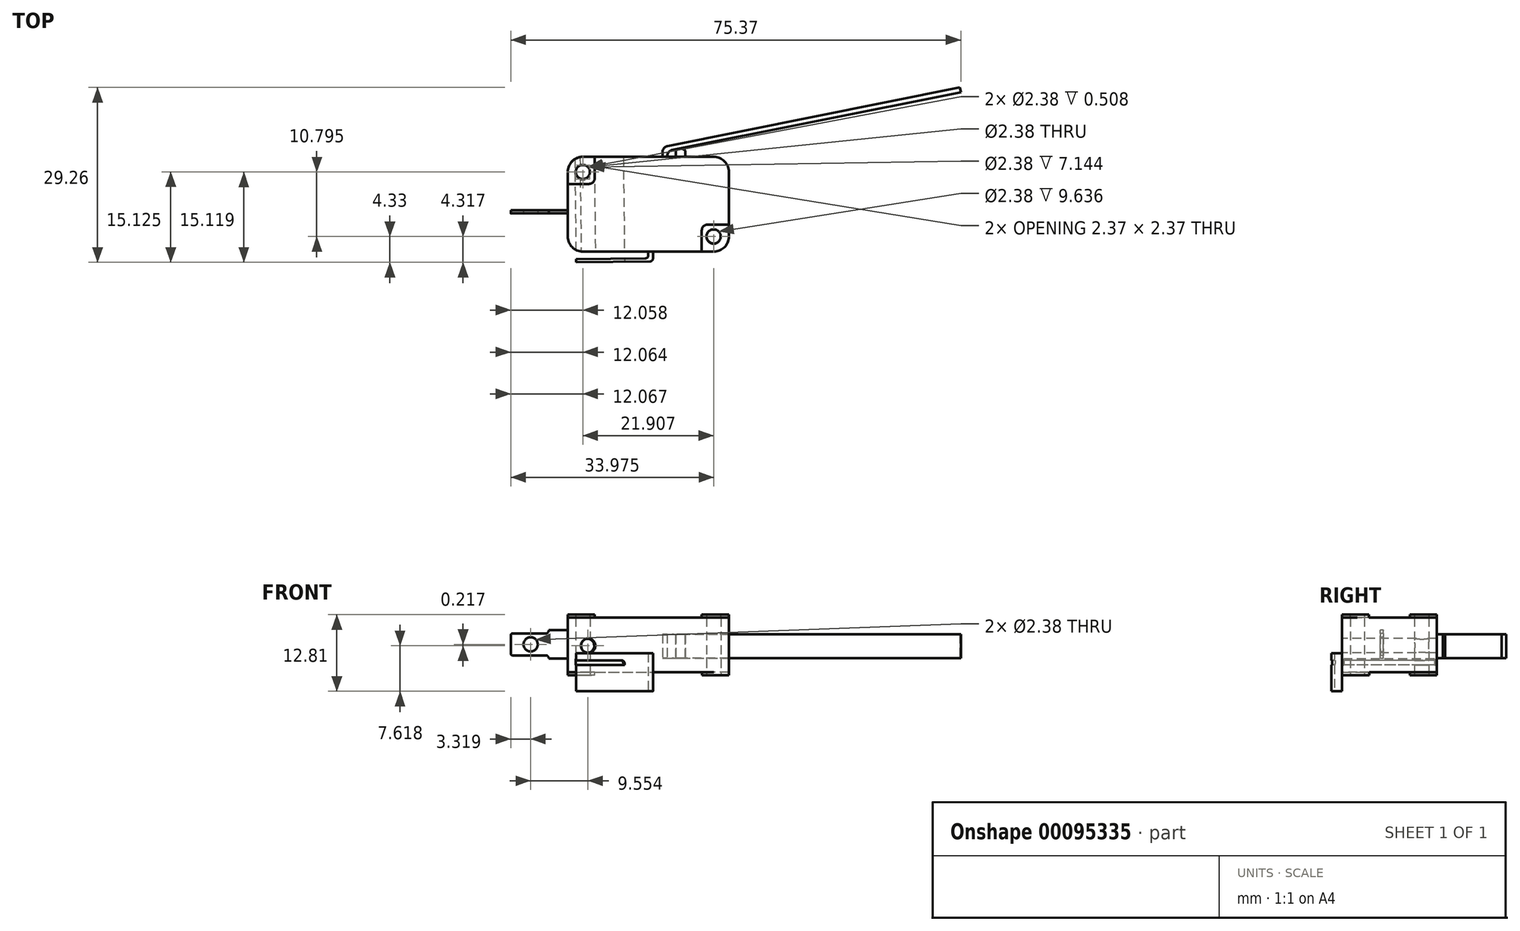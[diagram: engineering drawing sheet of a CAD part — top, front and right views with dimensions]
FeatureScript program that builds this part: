
annotation { "Feature Type Name" : "Feature", "Feature Type Description" : "" }
export const myFeature = defineFeature(function(context is Context, id is Id, definition is map)
    precondition{}
    {
        {
            var Q0;
            Q0=qCreatedBy(makeId("Top.planeOp"),FACE);
            var sketch = newSketch(context, id + "F0", { "sketchPlane" : qUnion([Q0])});
            skLineSegment(sketch, "E0.bottom", {"start": v(-22.21, 9.46) * mm, "end": v(-0.3, 9.46) * mm});
            skLineSegment(sketch, "E0.top", {"start": v(-22.21, -6.42) * mm, "end": v(-0.3, -6.42) * mm});
            skLineSegment(sketch, "E0.left", {"start": v(-24.75, 6.92) * mm, "end": v(-24.75, -3.88) * mm});
            skLineSegment(sketch, "E0.right", {"start": v(2.23, 6.92) * mm, "end": v(2.23, -3.88) * mm});
            skPoint(sketch, "E1.visualSharp", {"position": v(-24.75, 9.46) * mm});
            skArc(sketch, "E1.filletArc", {"start": v(-22.21, 9.46) * mm, "mid": v(-24, 8.71) * mm, "end": v(-24.75, 6.92) * mm});
            skPoint(sketch, "E2.visualSharp", {"position": v(2.23, 9.46) * mm});
            skArc(sketch, "E2.filletArc", {"start": v(2.23, 6.92) * mm, "mid": v(1.5, 8.71) * mm, "end": v(-0.3, 9.46) * mm});
            skPoint(sketch, "E3.visualSharp", {"position": v(2.23, -6.42) * mm});
            skArc(sketch, "E3.filletArc", {"start": v(-0.3, -6.42) * mm, "mid": v(1.5, -5.68) * mm, "end": v(2.23, -3.88) * mm});
            skPoint(sketch, "E4.visualSharp", {"position": v(-24.75, -6.42) * mm});
            skArc(sketch, "E4.filletArc", {"start": v(-24.75, -3.88) * mm, "mid": v(-24, -5.68) * mm, "end": v(-22.21, -6.42) * mm});
            skCircle(sketch, "E5", {"center": v(-22.21, 6.92) * mm, "radius": 1.2 * mm});
            skCircle(sketch, "E6", {"center": v(-0.3, -3.88) * mm, "radius": 1.2 * mm});
            skSolve(sketch);
        }
        {
            var Q0;
            Q0 = qSketchRegion(id + "F0", true);
            extrude(context, id + "F1", {"entities" : qUnion([Q0]), "depth" : 9.13 * mm});
        }
        {
            var Q0;
            Q0=makeQuery(id+"F1.opExtrude","CAP_FACE",FACE,{"disambiguationData":[OSD([sQuery(id+"F0.wireOp",EDGE,"E0.bottom"),sQuery(id+"F0.wireOp",EDGE,"E0.top"),sQuery(id+"F0.wireOp",EDGE,"E0.left"),sQuery(id+"F0.wireOp",EDGE,"E0.right"),sQuery(id+"F0.wireOp",EDGE,"E1.filletArc"),sQuery(id+"F0.wireOp",EDGE,"E2.filletArc"),sQuery(id+"F0.wireOp",EDGE,"E3.filletArc"),sQuery(id+"F0.wireOp",EDGE,"E4.filletArc"),sQuery(id+"F0.wireOp",EDGE,"E5"),sQuery(id+"F0.wireOp",EDGE,"E6")])],"isStart":true});
            cPlane(context, id + "F2", {"entities" : qUnion([Q0]), "cplaneType" : CPlaneType.OFFSET, "offset" : 2.38 * mm, "oppositeDirection" : true, "width" : 152.4 * mm, "height" : 152.4 * mm});
        }
        {
            var Q0;
            Q0=qCreatedBy(id+"F2.planeOp",FACE);
            var sketch = newSketch(context, id + "F3", { "sketchPlane" : qUnion([Q0])});
            skLineSegment(sketch, "E7", {"start": v(-8.88, -9.48) * mm, "end": v(-8.88, -11.07) * mm});
            skLineSegment(sketch, "E8", {"start": v(-8.88, -11.07) * mm, "end": v(40.93, -21.05) * mm});
            skLineSegment(sketch, "E9", {"start": v(40.93, -21.05) * mm, "end": v(41.09, -20.28) * mm});
            skLineSegment(sketch, "E10", {"start": v(41.09, -20.28) * mm, "end": v(-8.08, -10.42) * mm});
            skLineSegment(sketch, "E11", {"start": v(-8.08, -10.42) * mm, "end": v(-8.08, -9.48) * mm});
            skLineSegment(sketch, "E12", {"start": v(-8.08, -9.48) * mm, "end": v(-8.88, -9.48) * mm});
            skSolve(sketch);
        }
        {
            var Q0;
            Q0 = qSketchRegion(id + "F3", true);
            extrude(context, id + "F4", {"entities" : qUnion([Q0]), "oppositeDirection" : true, "depth" : 3.97 * mm});
        }
        {
            var Q0;
            Q0=makeQuery(id+"F4.opExtrude","SWEPT_EDGE",EDGE,{"disambiguationData":[OSD([sQuery(id+"F3.wireOp",EDGE,"E7"),sQuery(id+"F3.wireOp",EDGE,"E8")])]});
            var Q1;
            Q1=makeQuery(id+"F4.opExtrude","SWEPT_EDGE",EDGE,{"disambiguationData":[OSD([sQuery(id+"F3.wireOp",EDGE,"E10"),sQuery(id+"F3.wireOp",EDGE,"E11")])]});
            fillet(context, id + "F5", {"entities" : qUnion([Q0, Q1]), "radius" : 1.02 * mm, "tangentPropagation" : true, "allowEdgeOverflow" : false});
        }
        {
            var Q0;
            Q0=makeQuery(id+"F1.opExtrude","CAP_FACE",FACE,{"disambiguationData":[OSD([sQuery(id+"F0.wireOp",EDGE,"E0.bottom"),sQuery(id+"F0.wireOp",EDGE,"E0.top"),sQuery(id+"F0.wireOp",EDGE,"E0.left"),sQuery(id+"F0.wireOp",EDGE,"E0.right"),sQuery(id+"F0.wireOp",EDGE,"E1.filletArc"),sQuery(id+"F0.wireOp",EDGE,"E2.filletArc"),sQuery(id+"F0.wireOp",EDGE,"E3.filletArc"),sQuery(id+"F0.wireOp",EDGE,"E4.filletArc"),sQuery(id+"F0.wireOp",EDGE,"E5"),sQuery(id+"F0.wireOp",EDGE,"E6")])],"isStart":false});
            var sketch = newSketch(context, id + "F6", { "sketchPlane" : qUnion([Q0])});
            skLineSegment(sketch, "E13.bottom", {"start": v(-22.22, 9.44) * mm, "end": v(-20.24, 9.44) * mm});
            skLineSegment(sketch, "E13.top", {"start": v(-2.3, -6.43) * mm, "end": v(-0.31, -6.43) * mm});
            skLineSegment(sketch, "E13.left", {"start": v(-24.76, 6.9) * mm, "end": v(-24.76, 4.92) * mm});
            skLineSegment(sketch, "E13.right", {"start": v(2.23, -1.9) * mm, "end": v(2.23, -3.9) * mm});
            skPoint(sketch, "E14.visualSharp", {"position": v(-24.76, 9.44) * mm});
            skArc(sketch, "E14.filletArc", {"start": v(-22.22, 9.44) * mm, "mid": v(-24.02, 8.7) * mm, "end": v(-24.76, 6.9) * mm});
            skPoint(sketch, "E15.visualSharp", {"position": v(2.23, 9.44) * mm});
            skPoint(sketch, "E16.visualSharp", {"position": v(2.23, -6.43) * mm});
            skArc(sketch, "E16.filletArc", {"start": v(-0.31, -6.43) * mm, "mid": v(1.48, -5.69) * mm, "end": v(2.23, -3.9) * mm});
            skPoint(sketch, "E17.visualSharp", {"position": v(-24.76, -6.43) * mm});
            skCircle(sketch, "E18", {"center": v(-22.22, 6.9) * mm, "radius": 1.2 * mm});
            skCircle(sketch, "E19", {"center": v(-0.31, -3.9) * mm, "radius": 1.2 * mm});
            skLineSegment(sketch, "E20.bottom", {"start": v(-1.37, -1.9) * mm, "end": v(2.23, -1.9) * mm});
            skLineSegment(sketch, "E20.left", {"start": v(-2.3, -2.84) * mm, "end": v(-2.3, -6.43) * mm});
            skLineSegment(sketch, "E21.top", {"start": v(-24.76, 4.92) * mm, "end": v(-21.17, 4.92) * mm});
            skLineSegment(sketch, "E21.right", {"start": v(-20.24, 9.44) * mm, "end": v(-20.24, 5.85) * mm});
            skPoint(sketch, "E22.visualSharp", {"position": v(-20.24, 4.92) * mm});
            skArc(sketch, "E22.filletArc", {"start": v(-21.17, 4.92) * mm, "mid": v(-20.51, 5.2) * mm, "end": v(-20.24, 5.85) * mm});
            skPoint(sketch, "E23.visualSharp", {"position": v(-2.3, -1.9) * mm});
            skArc(sketch, "E23.filletArc", {"start": v(-1.37, -1.9) * mm, "mid": v(-2.03, -2.18) * mm, "end": v(-2.3, -2.84) * mm});
            skSolve(sketch);
        }
        {
            var Q0;
            Q0 = qSketchRegion(id + "F6", true);
            extrude(context, id + "F7", {"entities" : qUnion([Q0]), "operationType" : NewBodyOperationType.ADD, "depth" : 0.5 * mm});
        }
        {
            var Q0;
            Q0=qCreatedBy(id+"F2.planeOp",FACE);
            var sketch = newSketch(context, id + "F8", { "sketchPlane" : qUnion([Q0])});
            skLineSegment(sketch, "E24.bottom", {"start": v(-5.04, -9.44) * mm, "end": v(-6.67, -9.44) * mm});
            skLineSegment(sketch, "E24.top", {"start": v(-5.04, -10.44) * mm, "end": v(-6.67, -10.44) * mm});
            skLineSegment(sketch, "E24.left", {"start": v(-5.04, -9.44) * mm, "end": v(-5.04, -10.44) * mm});
            skLineSegment(sketch, "E24.right", {"start": v(-6.67, -9.44) * mm, "end": v(-6.67, -10.44) * mm});
            skArc(sketch, "E25", {"start": v(-6.67, -10.44) * mm, "mid": v(-5.86, -10.82) * mm, "end": v(-5.04, -10.44) * mm});
            skSolve(sketch);
        }
        {
            var Q0;
            Q0 = qSketchRegion(id + "F8", true);
            extrude(context, id + "F9", {"entities" : qUnion([Q0]), "operationType" : NewBodyOperationType.ADD, "oppositeDirection" : true, "depth" : 3.97 * mm});
        }
        {
            var Q0;
            Q0=qCreatedBy(makeId("Top.planeOp"),FACE);
            cPlane(context, id + "F10", {"entities" : qUnion([Q0]), "cplaneType" : CPlaneType.OFFSET, "offset" : 2.75 / 406.4 * mm, "width" : 152.4 * mm, "height" : 152.4 * mm});
        }
        {
            var Q0;
            Q0=qCreatedBy(id+"F10.planeOp",FACE);
            var sketch = newSketch(context, id + "F11", { "sketchPlane" : qUnion([Q0])});
            skLineSegment(sketch, "E26", {"start": v(-11.26, -6.43) * mm, "end": v(-11.26, -7.55) * mm});
            skLineSegment(sketch, "E27", {"start": v(-23.36, -8.2) * mm, "end": v(-23.36, -7.7) * mm});
            skLineSegment(sketch, "E28", {"start": v(-23.36, -8.2) * mm, "end": v(-10.47, -8.05) * mm});
            skLineSegment(sketch, "E29", {"start": v(-10.47, -8.05) * mm, "end": v(-10.47, -6.43) * mm});
            skLineSegment(sketch, "E30", {"start": v(-11.26, -6.43) * mm, "end": v(-10.47, -6.43) * mm});
            skLineSegment(sketch, "E31", {"start": v(-10.47, -7.55) * mm, "end": v(-10.47, -6.43) * mm});
            skLineSegment(sketch, "E32", {"start": v(-23.36, -7.7) * mm, "end": v(-11.26, -7.55) * mm});
            skSolve(sketch);
        }
        {
            var Q0;
            Q0=makeQuery(id+"F11.imprint","IMPRINT",FACE,{"disambiguationData":[TD([[makeQuery(id+"F11.imprint","IMPRINT",EDGE,{"derivedFrom":sQuery(id+"F11.wireOp",EDGE,"E26")}),1.0]])]});
            extrude(context, id + "F12", {"entities" : qUnion([Q0]), "depth" : 3.17 * mm, "hasSecondDirection" : true, "secondDirectionOppositeDirection" : true, "secondDirectionDepth" : 3.17 * mm});
        }
        {
            var Q0;
            {var subQ0=sQuery(id+"F11.wireOp",EDGE,"E28");Q0=makeQuery(id+"FmFe5163YoJR6j5_2.boolean.opBoolean","MERGE",FACE,{"derivedFrom":[makeQuery(id+"F12.opExtrude","SWEPT_FACE",FACE,{"disambiguationData":[OSD([subQ0])]}),makeQuery(id+"FmFe5163YoJR6j5_2.opExtrude","SWEPT_FACE",FACE,{"disambiguationData":[OSD([subQ0])]})]});}
            var sketch = newSketch(context, id + "F13", { "sketchPlane" : qUnion([Q0])});
            skCircle(sketch, "E33", {"center": v(-22.31, 4.41) * mm, "radius": 0.82 * mm});
            skSolve(sketch);
        }
        {
            var Q0;
            Q0=makeQuery(id+"F13.imprint","IMPRINT",FACE,{"disambiguationData":[TD([[makeQuery(id+"F13.imprint","IMPRINT",EDGE,{"derivedFrom":sQuery(id+"F13.wireOp",EDGE,"E33")}),1.0]])]});
            extrude(context, id + "F14", {"entities" : qUnion([Q0]), "operationType" : NewBodyOperationType.REMOVE, "oppositeDirection" : true, "depth" : 0.5 * mm});
        }
        {
            var Q0;
            Q0=qCreatedBy(makeId("Front.planeOp"),FACE);
            cPlane(context, id + "F15", {"entities" : qUnion([Q0]), "cplaneType" : CPlaneType.OFFSET, "offset" : 0.03 * mm, "width" : 152.4 * mm, "height" : 152.4 * mm});
        }
        {
            var Q0;
            Q0=qCreatedBy(id+"F15.planeOp",FACE);
            var sketch = newSketch(context, id + "F16", { "sketchPlane" : qUnion([Q0])});
            skLineSegment(sketch, "E34", {"start": v(-24.75, 2.28) * mm, "end": v(-24.75, 7.05) * mm});
            skLineSegment(sketch, "E35", {"start": v(-24.75, 7.05) * mm, "end": v(-27.93, 7.05) * mm});
            skLineSegment(sketch, "E36", {"start": v(-34.28, 6.24) * mm, "end": v(-34.28, 3.1) * mm});
            skLineSegment(sketch, "E37", {"start": v(-27.93, 2.28) * mm, "end": v(-24.75, 2.28) * mm});
            skCircle(sketch, "E38", {"center": v(-30.96, 4.66) * mm, "radius": 1.2 * mm});
            skPoint(sketch, "E39", {"position": v(-34.28, 4.66) * mm});
            skLineSegment(sketch, "E40", {"start": v(-27.93, 7.05) * mm, "end": v(-27.93, 6.5) * mm});
            skLineSegment(sketch, "E41", {"start": v(-27.93, 2.84) * mm, "end": v(-27.93, 2.28) * mm});
            skLineSegment(sketch, "E42", {"start": v(-27.93, 6.5) * mm, "end": v(-34.02, 6.5) * mm});
            skLineSegment(sketch, "E43", {"start": v(-27.93, 2.84) * mm, "end": v(-34.02, 2.84) * mm});
            skPoint(sketch, "E44.newPointB", {"position": v(-34.28, 7.05) * mm});
            skArc(sketch, "E44.filletArc", {"start": v(-34.02, 6.5) * mm, "mid": v(-34.2, 6.42) * mm, "end": v(-34.28, 6.24) * mm});
            skPoint(sketch, "E45.newPointB", {"position": v(-34.28, 2.28) * mm});
            skArc(sketch, "E45.filletArc", {"start": v(-34.28, 3.1) * mm, "mid": v(-34.2, 2.91) * mm, "end": v(-34.02, 2.84) * mm});
            skSolve(sketch);
        }
        {
            var Q0;
            Q0=makeQuery(id+"F16.imprint","IMPRINT",FACE,{"disambiguationData":[TD([[makeQuery(id+"F16.imprint","IMPRINT",EDGE,{"derivedFrom":sQuery(id+"F16.wireOp",EDGE,"E34")}),1.0]])]});
            extrude(context, id + "F17", {"entities" : qUnion([Q0]), "oppositeDirection" : true, "depth" : 0.5 * mm});
        }
        {
            var Q0;
            Q0=makeQuery(id+"F12.opExtrude","SWEPT_FACE",FACE,{"disambiguationData":[OSD([sQuery(id+"F11.wireOp",EDGE,"E28")])]});
            var sketch = newSketch(context, id + "F18", { "sketchPlane" : qUnion([Q0])});
            skCircle(sketch, "E46", {"center": v(-21.39, 4.45) * mm, "radius": 1.2 * mm});
            skLineSegment(sketch, "E47", {"start": v(-15.32, 7.54) * mm, "end": v(-15.32, 6.75) * mm});
            skLineSegment(sketch, "E48", {"start": v(-15.32, 1.98) * mm, "end": v(-15.32, 1.2) * mm});
            skLineSegment(sketch, "E49", {"start": v(-15.32, 6.75) * mm, "end": v(-23.2, 6.75) * mm});
            skLineSegment(sketch, "E50", {"start": v(-15.32, 1.98) * mm, "end": v(-23.2, 1.98) * mm});
            skLineSegment(sketch, "E51", {"start": v(-23.45, 6.75) * mm, "end": v(-23.45, 7.54) * mm});
            skLineSegment(sketch, "E52", {"start": v(-23.45, 7.54) * mm, "end": v(-15.32, 7.54) * mm});
            skLineSegment(sketch, "E53", {"start": v(-23.45, 1.98) * mm, "end": v(-23.45, 1.2) * mm});
            skLineSegment(sketch, "E54", {"start": v(-23.45, 1.2) * mm, "end": v(-15.32, 1.2) * mm});
            skLineSegment(sketch, "E55", {"start": v(-23.45, 6.5) * mm, "end": v(-23.45, 2.24) * mm});
            skPoint(sketch, "E56.visualSharp", {"position": v(-23.45, 6.75) * mm});
            skArc(sketch, "E56.filletArc", {"start": v(-23.2, 6.75) * mm, "mid": v(-23.38, 6.67) * mm, "end": v(-23.45, 6.5) * mm});
            skPoint(sketch, "E57.visualSharp", {"position": v(-23.45, 1.98) * mm});
            skArc(sketch, "E57.filletArc", {"start": v(-23.45, 2.24) * mm, "mid": v(-23.38, 2.06) * mm, "end": v(-23.2, 1.98) * mm});
            skSolve(sketch);
        }
        {
            var Q0;
            Q0 = qSketchRegion(id + "F18", true);
            var Q1;
            Q1=makeQuery(id+"F18.imprint","IMPRINT",FACE,{"disambiguationData":[TD([[makeQuery(id+"F18.imprint","IMPRINT",EDGE,{"derivedFrom":sQuery(id+"F18.wireOp",EDGE,"E47")}),-1.0]])]});
            var Q2;
            Q2=makeQuery(id+"F18.imprint","IMPRINT",FACE,{"disambiguationData":[TD([[makeQuery(id+"F18.imprint","IMPRINT",EDGE,{"derivedFrom":sQuery(id+"F18.wireOp",EDGE,"E48")}),-1.0]])]});
            extrude(context, id + "F19", {"entities" : qUnion([Q0, Q1, Q2]), "operationType" : NewBodyOperationType.REMOVE, "oppositeDirection" : true, "depth" : 25.4 * mm});
        }
        {
            var Q0;
            Q0=makeQuery(id+"F19.boolean.opBoolean","COPY",EDGE,{"derivedFrom":makeQuery(id+"F19.opExtrude","SWEPT_EDGE",EDGE,{"disambiguationData":[OSD([sQuery(id+"F18.wireOp",EDGE,"E47"),sQuery(id+"F18.wireOp",EDGE,"E49")])]})});
            var Q1;
            Q1=makeQuery(id+"F19.boolean.opBoolean","COPY",EDGE,{"derivedFrom":makeQuery(id+"F19.opExtrude","SWEPT_EDGE",EDGE,{"disambiguationData":[OSD([sQuery(id+"F18.wireOp",EDGE,"E48"),sQuery(id+"F18.wireOp",EDGE,"E50")])]})});
            var Q2;
            Q2=makeQuery(id+"F12.opExtrude","SWEPT_EDGE",EDGE,{"disambiguationData":[OSD([sQuery(id+"F11.wireOp",EDGE,"E28"),sQuery(id+"F11.wireOp",EDGE,"E29")])]});
            var Q3;
            Q3=makeQuery(id+"F12.opExtrude","SWEPT_EDGE",EDGE,{"disambiguationData":[OSD([sQuery(id+"F11.wireOp",EDGE,"E26"),sQuery(id+"F11.wireOp",EDGE,"E32")])]});
            fillet(context, id + "F20", {"entities" : qUnion([Q0, Q1, Q2, Q3]), "radius" : 0.5 * mm, "tangentPropagation" : true, "allowEdgeOverflow" : false});
        }
        {
            var Q0;
            Q0=makeQuery(id+"F17.opExtrude","SWEPT_EDGE",EDGE,{"disambiguationData":[OSD([sQuery(id+"F16.wireOp",EDGE,"E40"),sQuery(id+"F16.wireOp",EDGE,"E42")])]});
            var Q1;
            Q1=makeQuery(id+"F17.opExtrude","SWEPT_EDGE",EDGE,{"disambiguationData":[OSD([sQuery(id+"F16.wireOp",EDGE,"E41"),sQuery(id+"F16.wireOp",EDGE,"E43")])]});
            fillet(context, id + "F21", {"entities" : qUnion([Q0, Q1]), "radius" : 0.5 * mm, "tangentPropagation" : true, "allowEdgeOverflow" : false});
        }
        {
            var Q0;
            Q0=makeQuery(id+"F1.opExtrude","CAP_FACE",FACE,{"disambiguationData":[OSD([sQuery(id+"F0.wireOp",EDGE,"E0.bottom"),sQuery(id+"F0.wireOp",EDGE,"E0.top"),sQuery(id+"F0.wireOp",EDGE,"E0.left"),sQuery(id+"F0.wireOp",EDGE,"E0.right"),sQuery(id+"F0.wireOp",EDGE,"E1.filletArc"),sQuery(id+"F0.wireOp",EDGE,"E2.filletArc"),sQuery(id+"F0.wireOp",EDGE,"E3.filletArc"),sQuery(id+"F0.wireOp",EDGE,"E4.filletArc"),sQuery(id+"F0.wireOp",EDGE,"E5"),sQuery(id+"F0.wireOp",EDGE,"E6")])],"isStart":true});
            var sketch = newSketch(context, id + "F22", { "sketchPlane" : qUnion([Q0])});
            skPoint(sketch, "E58.visualSharp", {"position": v(19.76, 6.42) * mm});
            skPoint(sketch, "E59.visualSharp", {"position": v(-6.83, -9.46) * mm});
            skArc(sketch, "E60.MirrorCS", {"start": v(-22.21, -9.46) * mm, "mid": v(-24, -8.71) * mm, "end": v(-24.75, -6.92) * mm});
            skLineSegment(sketch, "E61.MirrorCS", {"start": v(-24.75, -4.93) * mm, "end": v(-24.75, -6.92) * mm});
            skLineSegment(sketch, "E62.MirrorCS", {"start": v(-21.16, -4.93) * mm, "end": v(-24.75, -4.93) * mm});
            skArc(sketch, "E63.MirrorCS", {"start": v(-21.16, -4.93) * mm, "mid": v(-20.5, -5.2) * mm, "end": v(-20.23, -5.86) * mm});
            skLineSegment(sketch, "E64.MirrorCS", {"start": v(-20.23, -5.86) * mm, "end": v(-20.23, -9.46) * mm});
            skLineSegment(sketch, "E65.MirrorCS", {"start": v(-20.23, -9.46) * mm, "end": v(-22.21, -9.46) * mm});
            skCircle(sketch, "E66.MirrorC", {"center": v(-22.21, -6.92) * mm, "radius": 1.2 * mm});
            skSolve(sketch);
        }
        {
            var Q0;
            Q0 = qSketchRegion(id + "F22", true);
            extrude(context, id + "F23", {"entities" : qUnion([Q0]), "operationType" : NewBodyOperationType.ADD, "depth" : 0.5 * mm});
        }
        {
            var Q0;
            Q0=makeQuery(id+"F1.opExtrude","CAP_FACE",FACE,{"disambiguationData":[OSD([sQuery(id+"F0.wireOp",EDGE,"E0.bottom"),sQuery(id+"F0.wireOp",EDGE,"E0.top"),sQuery(id+"F0.wireOp",EDGE,"E0.left"),sQuery(id+"F0.wireOp",EDGE,"E0.right"),sQuery(id+"F0.wireOp",EDGE,"E1.filletArc"),sQuery(id+"F0.wireOp",EDGE,"E2.filletArc"),sQuery(id+"F0.wireOp",EDGE,"E3.filletArc"),sQuery(id+"F0.wireOp",EDGE,"E4.filletArc"),sQuery(id+"F0.wireOp",EDGE,"E5"),sQuery(id+"F0.wireOp",EDGE,"E6")])],"isStart":true});
            var sketch = newSketch(context, id + "F24", { "sketchPlane" : qUnion([Q0])});
            skPoint(sketch, "E67.visualSharp", {"position": v(6.35, 6.41) * mm});
            skCircle(sketch, "E68.MirrorC", {"center": v(-0.3, 3.88) * mm, "radius": 1.2 * mm});
            skLineSegment(sketch, "E69.MirrorCS", {"start": v(-2.3, 6.42) * mm, "end": v(-2.29, 2.83) * mm});
            skArc(sketch, "E70.MirrorCS", {"start": v(-1.36, 1.9) * mm, "mid": v(-2.02, 2.17) * mm, "end": v(-2.29, 2.83) * mm});
            skLineSegment(sketch, "E71.MirrorCS", {"start": v(2.24, 1.9) * mm, "end": v(-1.36, 1.9) * mm});
            skLineSegment(sketch, "E72.MirrorCS", {"start": v(2.23, 3.88) * mm, "end": v(2.24, 1.9) * mm});
            skArc(sketch, "E73.MirrorCS", {"start": v(-0.3, 6.42) * mm, "mid": v(1.49, 5.68) * mm, "end": v(2.23, 3.88) * mm});
            skLineSegment(sketch, "E74.MirrorCS", {"start": v(-0.3, 6.42) * mm, "end": v(-2.3, 6.42) * mm});
            skSolve(sketch);
        }
        {
            var Q0;
            Q0 = qSketchRegion(id + "F24", true);
            extrude(context, id + "F25", {"entities" : qUnion([Q0]), "operationType" : NewBodyOperationType.ADD, "depth" : 0.5 * mm});
        }
    });
